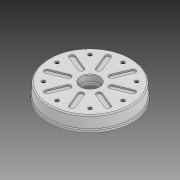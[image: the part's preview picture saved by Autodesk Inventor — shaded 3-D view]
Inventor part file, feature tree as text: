
AUTODESK INVENTOR PART (.ipt)
format: ipt  version: 2020 (Build 240168000, 168)  size: 1,596,928 bytes
history: native  units: mm
features: other x11, extrude x6, sketch x6, pattern_circular x4, chamfer x2, fillet x2, revolve x1, imported_body x1
ambient origin geometry x8: Origin, YZ Plane, XZ Plane, XY Plane, X Axis, Y Axis, Z Axis, Center Point
bodies: Solid1 (feature_tree)
feature tree (33):
  other  "HD_mastersketch.ipt"
  other  "Blocks"
  revolve  "Revolution1"  [1 undecoded]
  extrude  "Extrusion1"  Depth=4.0mm TaperAngle=0.0deg
  extrude  "Extrusion3"  Depth=1.7mm
  pattern_circular  "Circular Pattern1"  Count=73 Angle=360.0deg
  chamfer  "Chamfer1"  Distance=3.2mm
  extrude  "Extrusion2"  Depth=1.0mm
  fillet  "Fillet1"  Radius=4.0mm
  pattern_circular  "Circular Pattern2"  Angle=45.0deg  [1 undecoded]
  extrude  "Extrusion5"  Depth=10.0mm TaperAngle=0.0deg
  fillet  "Fillet2"  Radius=0.5mm
  pattern_circular  "Circular Pattern3"  Count=68 Angle=360.0deg
  extrude  "Extrusion6"  Depth=1.0mm
  chamfer  "Chamfer2"  Distance=22.5mm
  pattern_circular  "Circular Pattern4"  [2 undecoded]
  extrude  "Extrusion7"  Depth=1.0mm TaperAngle=0.0deg
  other  "608 bearing"
  other  "Belt"
  other  "Rotor"
  imported_body  "Base"
  sketch  "Sketch5"  dims[d0=10.0mm d24=7.0mm d25=22.0mm d26=8.0mm]
  sketch  "Sketch6"  dims[d1=90.0deg d4=4.0mm d5=0.0mm]
  sketch  "Sketch7"  dims[d6=80.0mm d7=360.0deg d9=1.7mm]
  other  "M3NutDepth_bot"
  other  "BeltCutDepth_bot"
  other  "M3NutDepth_top"
  other  "BeltCutDepth_top"
  sketch  "Sketch10"  dims[d11=1.25mm]
  sketch  "Sketch11"  dims[d12=4.0mm d13=0.0mm]
  sketch  "Sketch12"  dims[d14=0.5mm d15=730.0mm d16=360.0deg d18=3.2mm d19=5.7mm d20=4.0mm d21=0.0mm d34=0.5mm d35=2.0mm d36=45.0deg d37=0.8mm d38=1.8mm d39=8.726646mm d40=0.523599mm d41=0.523599mm d42=0.523599mm d43=0.523599mm d44=0.523599mm d45=2.792527mm d46=0.523599mm d47=68.0mm d48=70.740362mm d49=1.780032mm d50=9.749343mm d51=7.969311mm d52=6.189278mm d53=4.409246mm d54=2.629213mm d55=0.523599mm d56=0.523599mm d57=0.523599mm d58=0.523599mm d59=0.523599mm d60=11.529376mm d61=13.309408mm d62=15.089441mm d63=16.869473mm d64=18.649506mm d65=0.523599mm d66=0.523599mm d67=20.429538mm d68=22.209571mm d69=0.243598mm d70=72.932651mm d71=10.0mm d72=0.0mm d73=0.5mm d74=680.0mm d75=360.0deg d78=15.0mm d79=22.5mm d80=2.0mm d81=1.0mm d82=0.0mm d83=0.3mm d84=1.0mm d85=45.0deg d86=80.0mm d87=360.0deg d89=10.0mm d90=0.0mm d91=1.0mm d92=0.5mm d93=0.872665mm d94=0.5mm d95=0.872665mm]
  other  "608 bearing:1"
  other  "608 bearing:2"
note: 4 required parameter values undecoded (feature->parameter linkage not recoverable at this tier; creation-order binding heuristic only, values carry confidence <= 0.55)